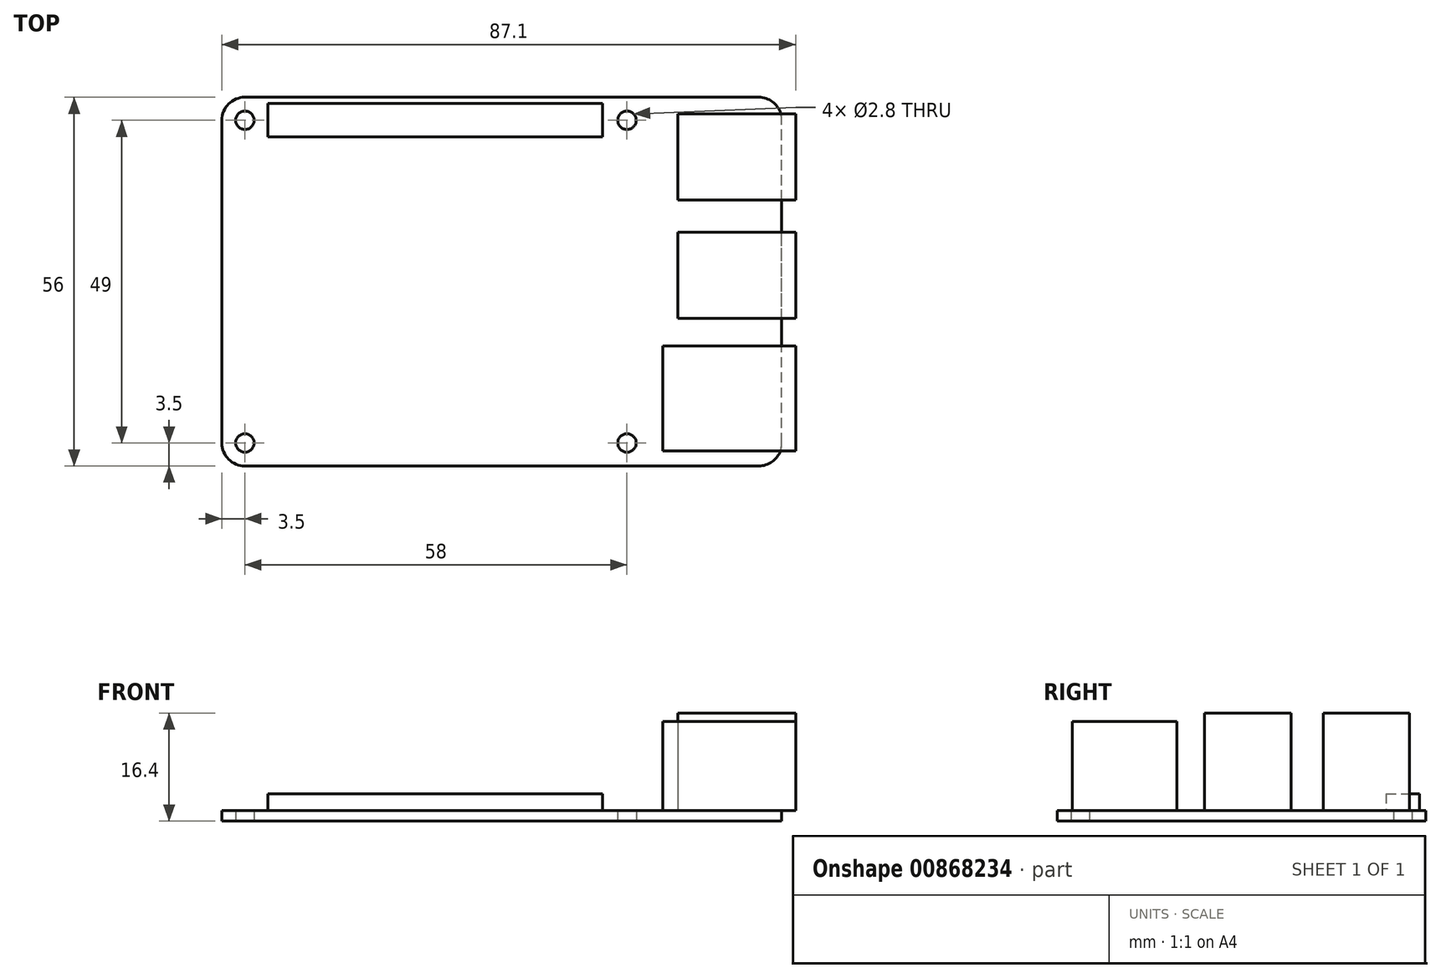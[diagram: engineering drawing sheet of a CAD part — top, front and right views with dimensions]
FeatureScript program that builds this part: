
annotation { "Feature Type Name" : "Feature", "Feature Type Description" : "" }
export const myFeature = defineFeature(function(context is Context, id is Id, definition is map)
    precondition{}
    {
        {
            var Q0;
            Q0=qCreatedBy(makeId("Top.planeOp"),FACE);
            var sketch = newSketch(context, id + "F0", { "sketchPlane" : qUnion([Q0])});
            skLineSegment(sketch, "E0.bottom", {"start": v(42.5, -28) * mm, "end": v(-42.5, -28) * mm});
            skLineSegment(sketch, "E0.top", {"start": v(42.5, 28) * mm, "end": v(-42.5, 28) * mm});
            skLineSegment(sketch, "E0.left", {"start": v(42.5, -28) * mm, "end": v(42.5, 28) * mm});
            skLineSegment(sketch, "E0.right", {"start": v(-42.5, -28) * mm, "end": v(-42.5, 28) * mm});
            skPoint(sketch, "E0.middle", {"position": v(0, 0) * mm});
            skPoint(sketch, "E1", {"position": v(-39, 24.5) * mm});
            skLineSegment(sketch, "E2", {"start": v(-42.5, 0) * mm, "end": v(42.5, 0) * mm, "construction": true});
            skPoint(sketch, "E3", {"position": v(19, 24.5) * mm});
            skLineSegment(sketch, "E4", {"start": v(19, 24.5) * mm, "end": v(-39, 24.5) * mm, "construction": true});
            skPoint(sketch, "E5.MirrorP", {"position": v(-39, -24.5) * mm});
            skPoint(sketch, "E6.MirrorP", {"position": v(19, -24.5) * mm});
            skSolve(sketch);
        }
        {
            var Q0;
            Q0 = qSketchRegion(id + "F0", true);
            extrude(context, id + "F1", {"entities" : qUnion([Q0]), "depth" : 1.6 * mm, "offsetDistance" : 25 * mm});
        }
        {
            var Q0;
            Q0=sQuery(id+"F0.wireOp",VERTEX,"E1");
            var Q1;
            Q1=sQuery(id+"F0.wireOp",VERTEX,"E3");
            var Q2;
            Q2=sQuery(id+"F0.wireOp",VERTEX,"E6.MirrorP");
            var Q3;
            Q3=sQuery(id+"F0.wireOp",VERTEX,"E5.MirrorP");
            var Q4;
            Q4=makeQuery(id+"F1.opExtrude","SWEPT_BODY",BODY,{"disambiguationData":[OSD([sQuery(id+"F0.wireOp",EDGE,"E0.bottom"),sQuery(id+"F0.wireOp",EDGE,"E0.top"),sQuery(id+"F0.wireOp",EDGE,"E0.left"),sQuery(id+"F0.wireOp",EDGE,"E0.right")])]});
            hole(context, id + "F2", {"style" : HoleStyle.SIMPLE, "endStyle" : HoleEndStyle.THROUGH, "oppositeDirection" : true, "holeDiameter" : 2.8 * mm, "majorDiameter" : 5 * mm, "isTappedThrough" : true, "tappedDepth" : 12 * mm, "tapClearance" : 3, "locations" : qUnion([Q0, Q1, Q2, Q3]), "scope" : qUnion([Q4])});
        }
        {
            var Q0;
            Q0=makeQuery(id+"F1.opExtrude","CAP_FACE",FACE,{"disambiguationData":[OSD([sQuery(id+"F0.wireOp",EDGE,"E0.bottom"),sQuery(id+"F0.wireOp",EDGE,"E0.top"),sQuery(id+"F0.wireOp",EDGE,"E0.left"),sQuery(id+"F0.wireOp",EDGE,"E0.right")])],"isStart":false});
            var sketch = newSketch(context, id + "F3", { "sketchPlane" : qUnion([Q0])});
            skLineSegment(sketch, "E7.bottom", {"start": v(15.3, 21.96) * mm, "end": v(-35.5, 21.96) * mm});
            skLineSegment(sketch, "E7.top", {"start": v(15.3, 27.04) * mm, "end": v(-35.5, 27.04) * mm});
            skLineSegment(sketch, "E7.left", {"start": v(15.3, 21.96) * mm, "end": v(15.3, 27.04) * mm});
            skLineSegment(sketch, "E7.right", {"start": v(-35.5, 21.96) * mm, "end": v(-35.5, 27.04) * mm});
            skPoint(sketch, "E7.middle", {"position": v(-10.1, 24.5) * mm});
            skLineSegment(sketch, "E8", {"start": v(-39, 24.5) * mm, "end": v(19, 24.5) * mm, "construction": true});
            skSolve(sketch);
        }
        {
            var Q0;
            Q0 = qSketchRegion(id + "F3", true);
            extrude(context, id + "F4", {"entities" : qUnion([Q0]), "operationType" : NewBodyOperationType.ADD, "depth" : 2.54 * mm, "offsetDistance" : 25 * mm});
        }
        {
            var Q0;
            Q0=makeQuery(id+"F1.opExtrude","CAP_FACE",FACE,{"disambiguationData":[OSD([sQuery(id+"F0.wireOp",EDGE,"E0.bottom"),sQuery(id+"F0.wireOp",EDGE,"E0.top"),sQuery(id+"F0.wireOp",EDGE,"E0.left"),sQuery(id+"F0.wireOp",EDGE,"E0.right")])],"isStart":false});
            var sketch = newSketch(context, id + "F5", { "sketchPlane" : qUnion([Q0])});
            skLineSegment(sketch, "E9.bottom", {"start": v(44.6, 12.4) * mm, "end": v(26.71, 12.4) * mm});
            skLineSegment(sketch, "E9.top", {"start": v(44.6, 25.5) * mm, "end": v(26.71, 25.5) * mm});
            skLineSegment(sketch, "E9.left", {"start": v(44.6, 12.4) * mm, "end": v(44.6, 25.5) * mm});
            skLineSegment(sketch, "E9.right", {"start": v(26.71, 12.4) * mm, "end": v(26.71, 25.5) * mm});
            skPoint(sketch, "E9.middle", {"position": v(35.66, 18.95) * mm});
            skLineSegment(sketch, "E10.bottom", {"start": v(44.6, -5.6) * mm, "end": v(26.71, -5.6) * mm});
            skLineSegment(sketch, "E10.top", {"start": v(44.6, 7.5) * mm, "end": v(26.71, 7.5) * mm});
            skLineSegment(sketch, "E10.left", {"start": v(44.6, -5.6) * mm, "end": v(44.6, 7.5) * mm});
            skLineSegment(sketch, "E10.right", {"start": v(26.71, -5.6) * mm, "end": v(26.71, 7.5) * mm});
            skPoint(sketch, "E10.middle", {"position": v(35.66, 0.95) * mm});
            skLineSegment(sketch, "E11", {"start": v(44.6, 12.4) * mm, "end": v(44.6, 7.5) * mm, "construction": true});
            skSolve(sketch);
        }
        {
            var Q0;
            Q0 = qSketchRegion(id + "F5", true);
            extrude(context, id + "F6", {"entities" : qUnion([Q0]), "operationType" : NewBodyOperationType.ADD, "depth" : 14.8 * mm, "offsetDistance" : 25 * mm});
        }
        {
            var Q0;
            Q0=makeQuery(id+"F1.opExtrude","CAP_FACE",FACE,{"disambiguationData":[OSD([sQuery(id+"F0.wireOp",EDGE,"E0.bottom"),sQuery(id+"F0.wireOp",EDGE,"E0.top"),sQuery(id+"F0.wireOp",EDGE,"E0.left"),sQuery(id+"F0.wireOp",EDGE,"E0.right")])],"isStart":false});
            var sketch = newSketch(context, id + "F7", { "sketchPlane" : qUnion([Q0])});
            skLineSegment(sketch, "E12.bottom", {"start": v(44.6, -25.7) * mm, "end": v(24.41, -25.7) * mm});
            skLineSegment(sketch, "E12.top", {"start": v(44.6, -9.8) * mm, "end": v(24.41, -9.8) * mm});
            skLineSegment(sketch, "E12.left", {"start": v(44.6, -25.7) * mm, "end": v(44.6, -9.8) * mm});
            skLineSegment(sketch, "E12.right", {"start": v(24.41, -25.7) * mm, "end": v(24.41, -9.8) * mm});
            skPoint(sketch, "E12.middle", {"position": v(34.5, -17.75) * mm});
            skSolve(sketch);
        }
        {
            var Q0;
            Q0 = qSketchRegion(id + "F7", true);
            extrude(context, id + "F8", {"entities" : qUnion([Q0]), "operationType" : NewBodyOperationType.ADD, "depth" : 13.5 * mm, "offsetDistance" : 25 * mm});
        }
        {
            var Q0;
            Q0=makeQuery(id+"F1.opExtrude","SWEPT_EDGE",EDGE,{"disambiguationData":[OSD([sQuery(id+"F0.wireOp",EDGE,"E0.bottom"),sQuery(id+"F0.wireOp",EDGE,"E0.right")])]});
            var Q1;
            Q1=makeQuery(id+"F1.opExtrude","SWEPT_EDGE",EDGE,{"disambiguationData":[OSD([sQuery(id+"F0.wireOp",EDGE,"E0.top"),sQuery(id+"F0.wireOp",EDGE,"E0.right")])]});
            var Q2;
            Q2=makeQuery(id+"F1.opExtrude","SWEPT_EDGE",EDGE,{"disambiguationData":[OSD([sQuery(id+"F0.wireOp",EDGE,"E0.bottom"),sQuery(id+"F0.wireOp",EDGE,"E0.left")])]});
            var Q3;
            Q3=makeQuery(id+"F1.opExtrude","SWEPT_EDGE",EDGE,{"disambiguationData":[OSD([sQuery(id+"F0.wireOp",EDGE,"E0.top"),sQuery(id+"F0.wireOp",EDGE,"E0.left")])]});
            fillet(context, id + "F9", {"entities" : qUnion([Q0, Q1, Q2, Q3]), "radius" : 3.5 * mm, "tangentPropagation" : true, "allowEdgeOverflow" : false});
        }
    });
